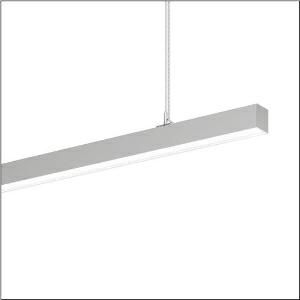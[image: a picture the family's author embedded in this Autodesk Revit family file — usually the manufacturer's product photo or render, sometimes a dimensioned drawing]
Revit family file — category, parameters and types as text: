
# Revit family: silica_r__21_51mx30dc49sb_4188
name_source: partatom
category: Lighting Fixtures
units: mm (PartAtom-declared; Revit-internal decimal feet)

## family parameters
Cut with Voids When Loaded = No
Host = Face
Light Source = No
Part Type = Normal
Room Calculation Point = No
Round Connector Dimension = Use Diameter
Shared = No

## types (1)
- --- (1 x LED, 10520 lm, 64.1 W, 4000K)
    Apparent Load = 64 VA
    CIE Flux Codes = 47 79 96 57 100
    Color Rendering = 80
    Color Temperature = 4000K
    Default Elevation = 1800 mm
    Description = Silica® 21, office luminaire, primary optical cover: cover, of PMMA, opal, light emission: direct/indirect distribution, primary light characteristic: symmetric, installation type: suspended mounting, LED, rated luminous flux: 10.520lm, luminous efficacy: 164lm/W, light colour: 840, colour temperature: 4000K, with terminal, 3+2-pole, max. 2.5mm², mains connection: 220..240V, AC, 50/60Hz, rated input power: 64.1W, luminaire housing, of aluminium, metallic grey (RAL 9006), length: 3.004mm, width: 53mm, height: 53mm, protection rating (complete): IP20, insulation class (complete): insulation class I (protective earthing), certification: CE, permissible operating ambient temperature: 0..+35°C, standard: EN 50419, packaging unit: 1 piece
    Height = 53 mm
    Lamp = 1 x LED
    Lamp Light Flux = 10520 lm
    Lamp Power = 64.1 W
    Lamp count = 1
    Length = 3004 mm
    Luminous efficacy = 164 lm/W
    Manufacturer = Siteco
    ModVariant = No
    Model = 51MX30DC49SB
    Mounting Place = Ceiling
    Mounting Type = Pendant
    Number of Poles = 1
    OnlyDefault = Yes
    Power Factor = 1
    Product Name = Silica® 21
    Product group = office luminaire | ceiling pendant
    ProductGroupID = 902
    Protection Class = Protection class I
    Protection Degree = IP 20
    RLX_Detail_Level = 1
    RLX_Emergency_Light_Flux = 0 lm
    RLX_Emergency_Type = 0
    RLX_Emergency_Type_DB = No
    RlxData = <blob elided: 23157 chars, md5=e462365b>
    Socket = socket
    Standby Power = 0 W
    System Light Flux = 10520 lm
    System Power = 64 W
    Type Comments = factory setting: luminous flux: 100 % | dim-lin: 254 | 218 mA
    Type Image = l_1335864.jpg
    URL = http://relux.com
    VarID = @adj_085951
    Voltage = 0 V
    Weight = 0.00 kg
    Width = 53 mm

## geometry (parser evidence)
native form markers: Blend x4, Sweep x11
no freeform markers — native parametric forms only
